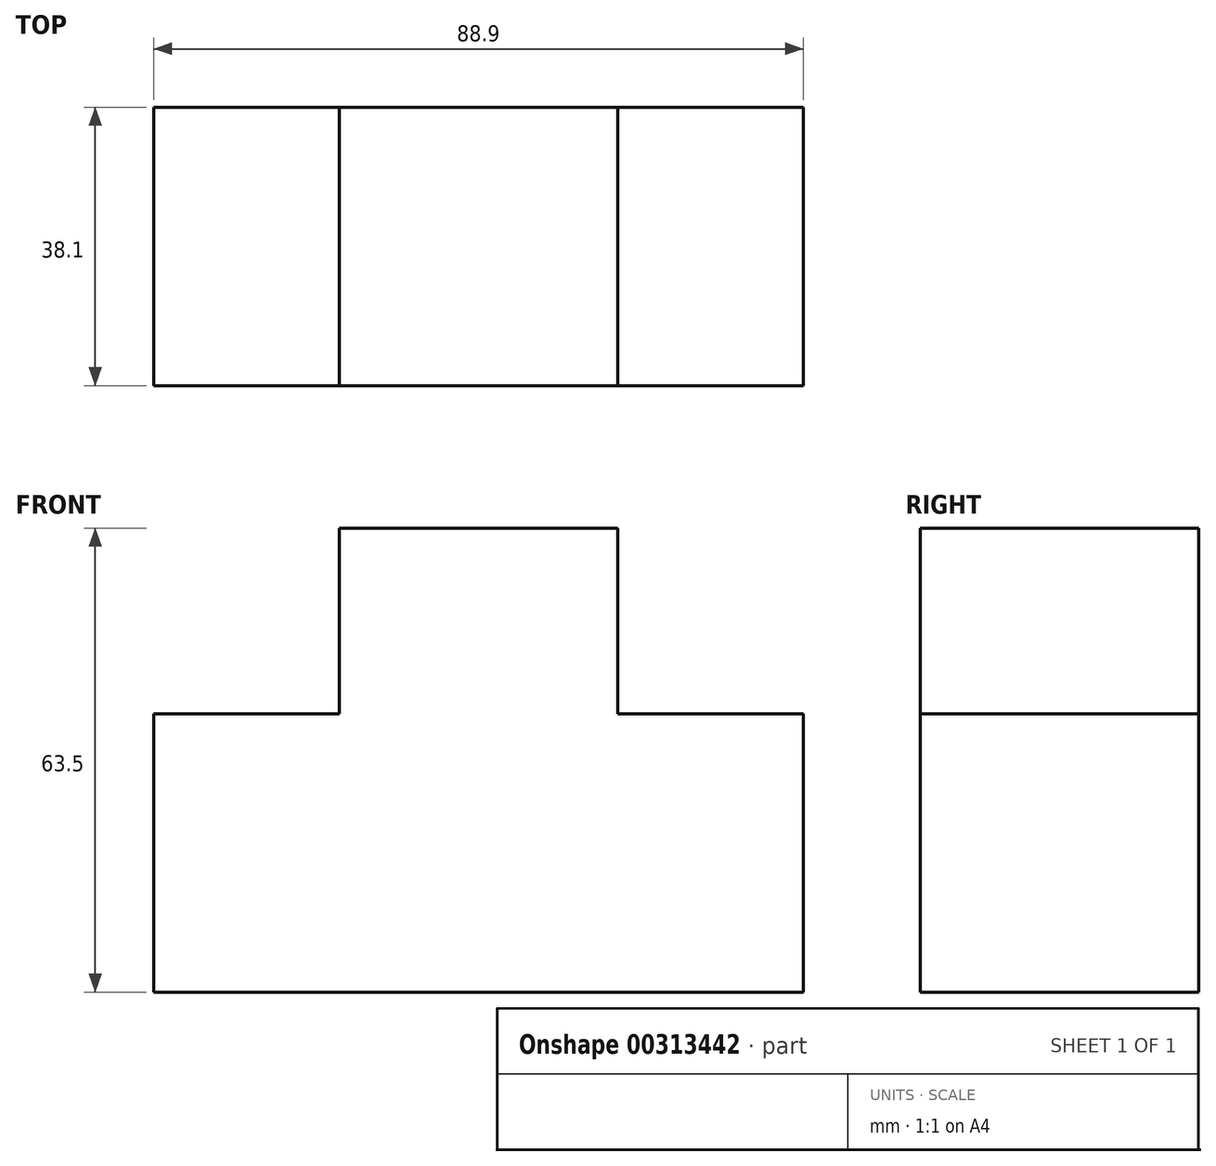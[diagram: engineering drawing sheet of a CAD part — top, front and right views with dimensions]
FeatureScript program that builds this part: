
annotation { "Feature Type Name" : "Feature", "Feature Type Description" : "" }
export const myFeature = defineFeature(function(context is Context, id is Id, definition is map)
    precondition{}
    {
        {
            var Q0;
            Q0=qCreatedBy(makeId("Front.planeOp"),FACE);
            var sketch = newSketch(context, id + "F0", { "sketchPlane" : qUnion([Q0])});
            skLineSegment(sketch, "E0", {"start": v(-44.99, -38.1) * mm, "end": v(43.91, -38.1) * mm});
            skLineSegment(sketch, "E1", {"start": v(43.91, -38.1) * mm, "end": v(43.91, 0) * mm});
            skLineSegment(sketch, "E2", {"start": v(43.91, 0) * mm, "end": v(18.51, 0) * mm});
            skLineSegment(sketch, "E3", {"start": v(18.51, 0) * mm, "end": v(18.51, 25.4) * mm});
            skLineSegment(sketch, "E4", {"start": v(18.51, 25.4) * mm, "end": v(-19.59, 25.4) * mm});
            skLineSegment(sketch, "E5", {"start": v(-19.59, 25.4) * mm, "end": v(-19.59, 0) * mm});
            skLineSegment(sketch, "E6", {"start": v(-19.59, 0) * mm, "end": v(-44.99, 0) * mm});
            skLineSegment(sketch, "E7", {"start": v(-44.99, 0) * mm, "end": v(-44.99, -38.1) * mm});
            skSolve(sketch);
        }
        {
            var Q0;
            Q0=makeQuery(id+"F0.imprint","IMPRINT",FACE,{"disambiguationData":[TD([[makeQuery(id+"F0.imprint","IMPRINT",EDGE,{"derivedFrom":sQuery(id+"F0.wireOp",EDGE,"E0")}),1.0]])]});
            extrude(context, id + "F1", {"entities" : qUnion([Q0]), "depth" : 38.1 * mm});
        }
    });
